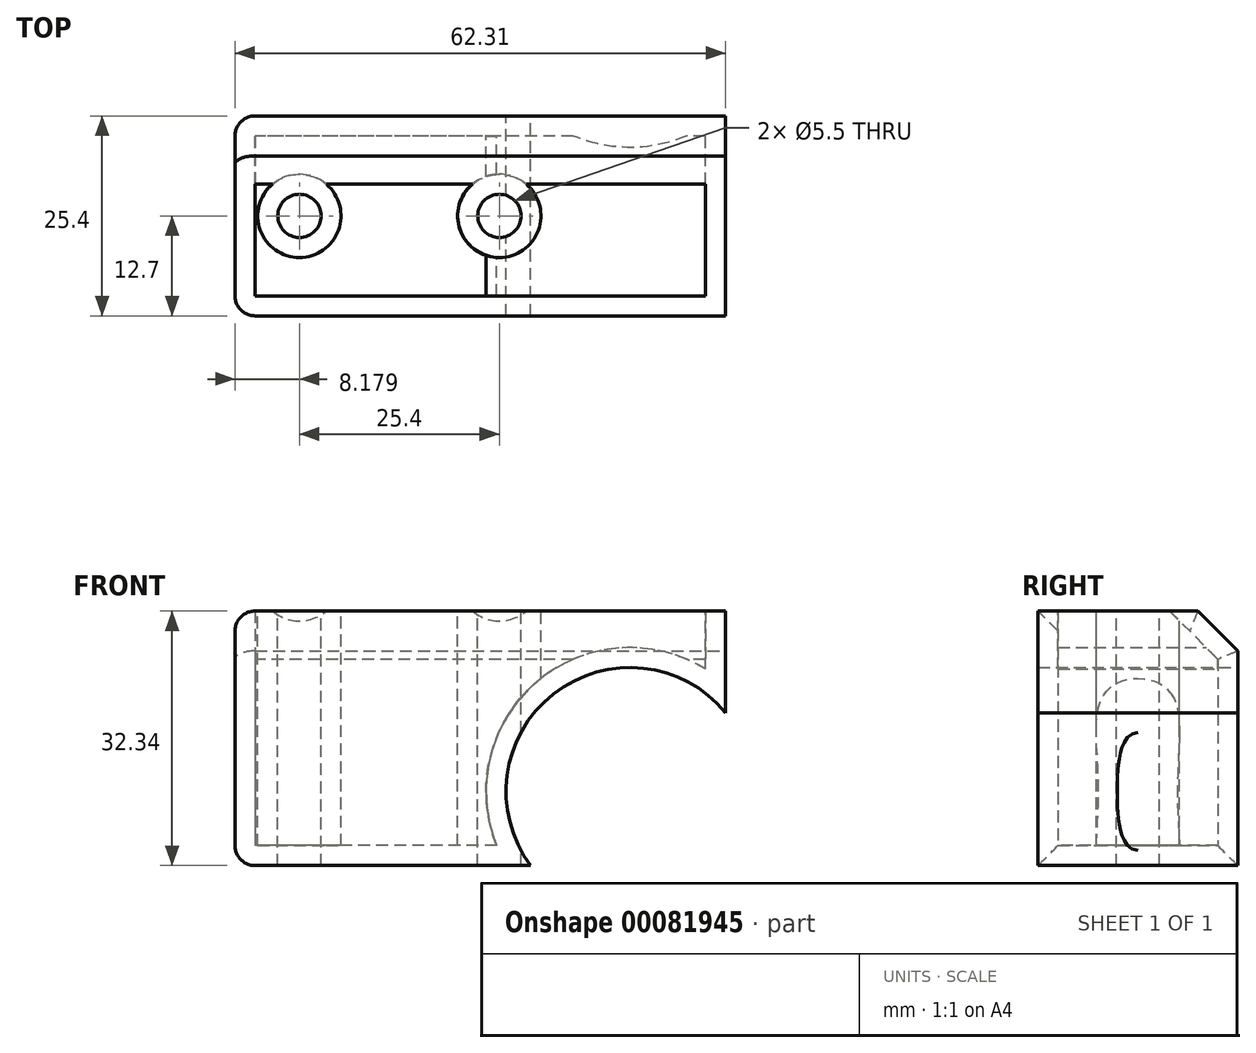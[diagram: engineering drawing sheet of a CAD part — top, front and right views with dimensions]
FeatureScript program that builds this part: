
annotation { "Feature Type Name" : "Feature", "Feature Type Description" : "" }
export const myFeature = defineFeature(function(context is Context, id is Id, definition is map)
    precondition{}
    {
        {
            var Q0;
            Q0=qCreatedBy(makeId("Front.planeOp"),FACE);
            var sketch = newSketch(context, id + "F0", { "sketchPlane" : qUnion([Q0])});
            skLineSegment(sketch, "E0.bottom", {"start": v(-24.75, 0) * mm, "end": v(-62.3, 0) * mm});
            skLineSegment(sketch, "E0.top", {"start": v(0, 32.34) * mm, "end": v(-62.3, 32.34) * mm});
            skLineSegment(sketch, "E0.left", {"start": v(0, 19.42) * mm, "end": v(0, 32.34) * mm});
            skLineSegment(sketch, "E0.right", {"start": v(-62.3, 0) * mm, "end": v(-62.3, 32.34) * mm});
            skCircle(sketch, "E1", {"center": v(-35.52, 18.04) * mm, "radius": 7.3 * mm});
            skArc(sketch, "E2", {"start": v(0, 19.42) * mm, "mid": v(-21.86, 21.8) * mm, "end": v(-24.75, 0) * mm});
            skSolve(sketch);
        }
        {
            var Q0;
            Q0=makeQuery(id+"F0.imprint","IMPRINT",FACE,{"disambiguationData":[TD([[makeQuery(id+"F0.imprint","IMPRINT",EDGE,{"derivedFrom":sQuery(id+"F0.wireOp",EDGE,"E0.bottom")}),-1.0]])]});
            var Q1;
            Q1=makeQuery(id+"F0.imprint","IMPRINT",FACE,{"disambiguationData":[TD([[makeQuery(id+"F0.imprint","IMPRINT",EDGE,{"derivedFrom":sQuery(id+"F0.wireOp",EDGE,"E1")}),1.0]])]});
            extrude(context, id + "F1", {"entities" : qUnion([Q0, Q1]), "depth" : 25.4 * mm});
        }
        {
            var Q0;
            Q0=makeQuery(id+"F1.opExtrude","SWEPT_FACE",FACE,{"disambiguationData":[OSD([sQuery(id+"F0.wireOp",EDGE,"E0.top")])]});
            var sketch = newSketch(context, id + "F2", { "sketchPlane" : qUnion([Q0])});
            skPoint(sketch, "E3", {"position": v(-54.13, -12.7) * mm});
            skPoint(sketch, "E4", {"position": v(-28.73, -12.7) * mm});
            skLineSegment(sketch, "E5.bottom", {"start": v(-42.91, -11.1) * mm, "end": v(-13.14, -11.1) * mm, "construction": true});
            skLineSegment(sketch, "E5.top", {"start": v(-42.91, -19.09) * mm, "end": v(-13.14, -19.09) * mm, "construction": true});
            skLineSegment(sketch, "E5.left", {"start": v(-42.91, -11.1) * mm, "end": v(-42.91, -19.09) * mm, "construction": true});
            skLineSegment(sketch, "E5.right", {"start": v(-13.14, -11.1) * mm, "end": v(-13.14, -19.09) * mm, "construction": true});
            skSolve(sketch);
        }
        {
            var Q0;
            Q0=sQuery(id+"F2.wireOp",VERTEX,"E3");
            var Q1;
            Q1=sQuery(id+"F2.wireOp",VERTEX,"E4");
            var Q2;
            Q2=makeQuery(id+"F1.opExtrude","SWEPT_BODY",BODY,{"disambiguationData":[OSD([sQuery(id+"F0.wireOp",EDGE,"E0.bottom"),sQuery(id+"F0.wireOp",EDGE,"E0.top"),sQuery(id+"F0.wireOp",EDGE,"E0.left"),sQuery(id+"F0.wireOp",EDGE,"E0.right"),sQuery(id+"F0.wireOp",EDGE,"E2")])]});
            hole(context, id + "F3", {"style" : HoleStyle.SIMPLE, "endStyle" : HoleEndStyle.THROUGH, "standardTappedOrClearance" : lookupTablePath({ "standard" : "ISO", "fit" : "Normal", "size" : "M5", "type" : "Clearance" }), "standardBlindInLast" : lookupTablePath({ "fit" : "Standard", "standard" : "ISO", "size" : "M5", "type" : "Clearance" }), "holeDiameter" : 5.5 * mm, "locations" : qUnion([Q0, Q1]), "scope" : qUnion([Q2]), "isTappedThrough" : true});
        }
        {
            var Q0;
            Q0=makeQuery(id+"F1.opExtrude","CAP_EDGE",EDGE,{"disambiguationData":[OSD([sQuery(id+"F0.wireOp",EDGE,"E0.top")])],"isStart":true});
            chamfer(context, id + "F4", {"entities" : qUnion([Q0]), "width" : 5.08 * mm, "tangentPropagation" : true});
        }
        {
            var Q0;
            Q0=makeQuery(id+"F1.opExtrude","SWEPT_FACE",FACE,{"disambiguationData":[OSD([sQuery(id+"F0.wireOp",EDGE,"E0.right")])]});
            fillet(context, id + "F5", {"entities" : qUnion([Q0]), "radius" : 2.54 * mm, "tangentPropagation" : true, "allowEdgeOverflow" : false});
        }
        {
            var Q0;
            Q0=makeQuery(id+"F1.opExtrude","SWEPT_FACE",FACE,{"disambiguationData":[OSD([sQuery(id+"F0.wireOp",EDGE,"E0.top")])]});
            shell(context, id + "F6", {"entities" : qUnion([Q0]), "thickness" : 2.54 * mm});
        }
    });
